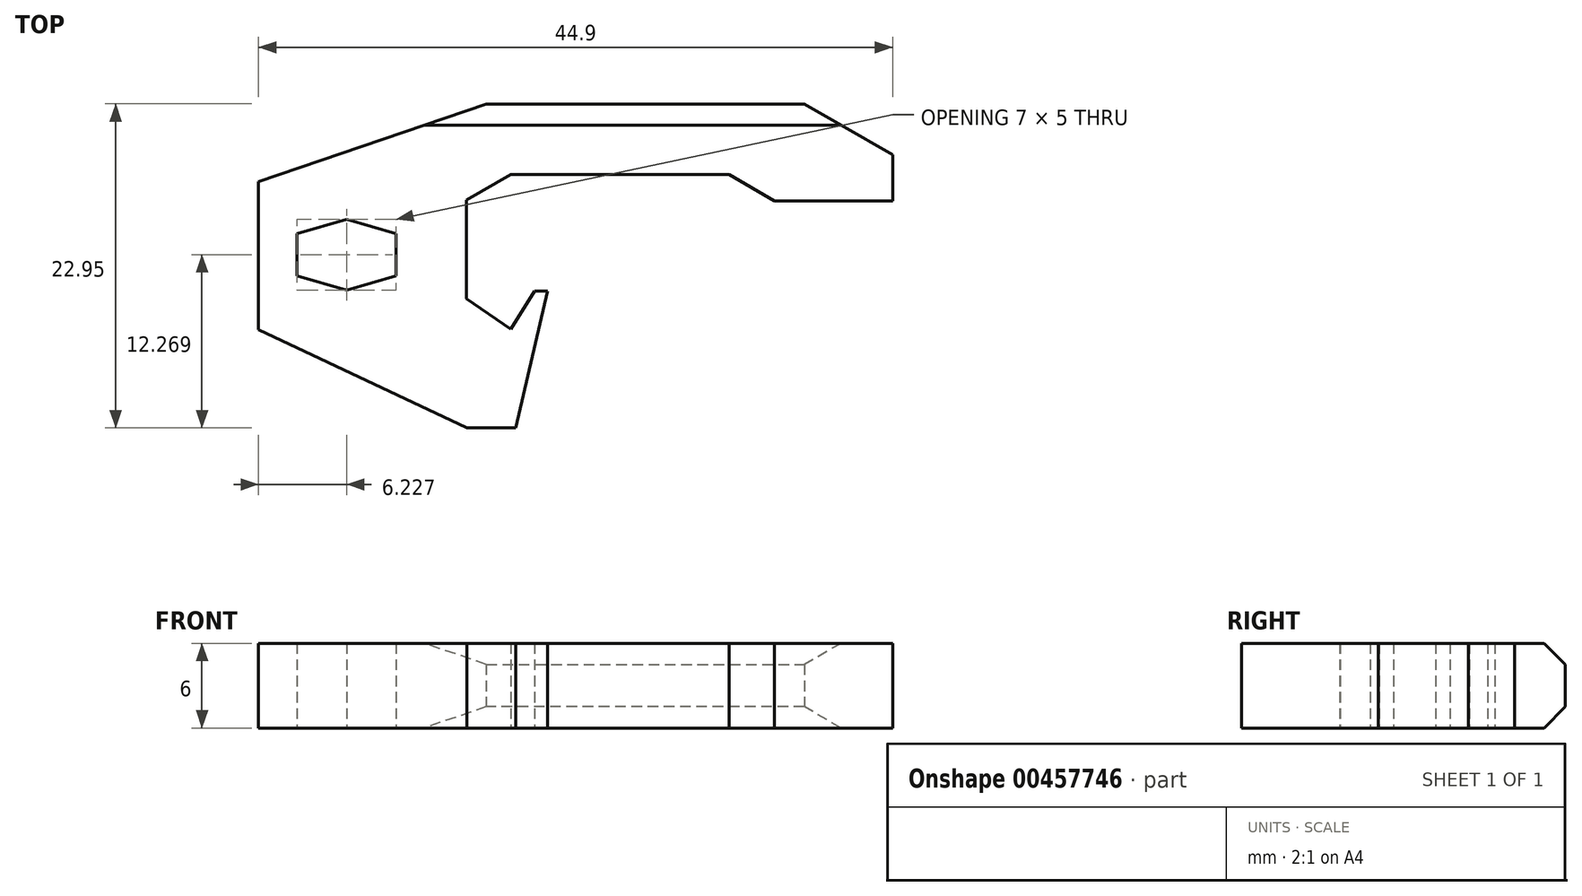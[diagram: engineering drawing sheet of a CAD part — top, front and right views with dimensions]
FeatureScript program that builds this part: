
annotation { "Feature Type Name" : "Feature", "Feature Type Description" : "" }
export const myFeature = defineFeature(function(context is Context, id is Id, definition is map)
    precondition{}
    {
        {
            var Q0;
            Q0=qCreatedBy(makeId("Top.planeOp"),FACE);
            var sketch = newSketch(context, id + "F0", { "sketchPlane" : qUnion([Q0])});
            skLineSegment(sketch, "E0", {"start": v(-1.74, 12.66) * mm, "end": v(20.78, 12.66) * mm});
            skLineSegment(sketch, "E1", {"start": v(20.78, 12.66) * mm, "end": v(32.67, 5.8) * mm});
            skLineSegment(sketch, "E2", {"start": v(32.67, 5.8) * mm, "end": v(18.67, 5.8) * mm});
            skLineSegment(sketch, "E3", {"start": v(18.67, 5.8) * mm, "end": v(15.44, 7.66) * mm});
            skLineSegment(sketch, "E4", {"start": v(15.44, 7.66) * mm, "end": v(0, 7.66) * mm});
            skLineSegment(sketch, "E5", {"start": v(0, 7.66) * mm, "end": v(-3.14, 5.84) * mm});
            skLineSegment(sketch, "E6", {"start": v(-3.14, 5.84) * mm, "end": v(-3.14, -1.15) * mm});
            skLineSegment(sketch, "E7", {"start": v(-3.14, -1.15) * mm, "end": v(0, -3.29) * mm});
            skLineSegment(sketch, "E8", {"start": v(0, -3.29) * mm, "end": v(1.66, -0.58) * mm});
            skLineSegment(sketch, "E9", {"start": v(1.66, -0.58) * mm, "end": v(2.58, -0.58) * mm});
            skLineSegment(sketch, "E10", {"start": v(2.58, -0.58) * mm, "end": v(0.33, -10.29) * mm});
            skLineSegment(sketch, "E11", {"start": v(0.33, -10.29) * mm, "end": v(-3.1, -10.29) * mm});
            skLineSegment(sketch, "E12", {"start": v(-3.1, -10.29) * mm, "end": v(-17.87, -3.32) * mm});
            skLineSegment(sketch, "E13", {"start": v(-17.87, -3.32) * mm, "end": v(-17.87, 7.14) * mm});
            skLineSegment(sketch, "E14", {"start": v(-17.87, 7.14) * mm, "end": v(-1.74, 12.66) * mm});
            skLineSegment(sketch, "E15", {"start": v(-15.14, 3.48) * mm, "end": v(-15.14, 0.48) * mm});
            skLineSegment(sketch, "E16", {"start": v(-15.14, 0.48) * mm, "end": v(-11.64, -0.52) * mm});
            skLineSegment(sketch, "E17", {"start": v(-11.64, -0.52) * mm, "end": v(-8.14, 0.48) * mm});
            skLineSegment(sketch, "E18", {"start": v(-8.14, 0.48) * mm, "end": v(-8.14, 3.48) * mm});
            skLineSegment(sketch, "E19", {"start": v(-8.14, 3.48) * mm, "end": v(-11.64, 4.48) * mm});
            skLineSegment(sketch, "E20", {"start": v(-11.64, 4.48) * mm, "end": v(-15.14, 3.48) * mm});
            skLineSegment(sketch, "E21", {"start": v(-11.64, 4.48) * mm, "end": v(-11.64, -0.52) * mm, "construction": true});
            skLineSegment(sketch, "E22", {"start": v(-15.14, 1.98) * mm, "end": v(-8.14, 1.98) * mm, "construction": true});
            skPoint(sketch, "E23", {"position": v(-11.64, 1.98) * mm});
            skLineSegment(sketch, "E24", {"start": v(27.03, 5.8) * mm, "end": v(27.03, 9.05) * mm});
            skLineSegment(sketch, "E25", {"start": v(-17.87, -2.78) * mm, "end": v(-13.3, -4.32) * mm});
            skLineSegment(sketch, "E26", {"start": v(-13.3, -4.32) * mm, "end": v(-3.1, -10.29) * mm});
            skSolve(sketch);
        }
        {
            var Q0;
            {var subQ0=sQuery(id+"F0.wireOp",EDGE,"E0");Q0=makeQuery(id+"F0.imprint","IMPRINT",FACE,{"disambiguationData":[TD([[makeQuery(id+"F0.imprint","IMPRINT",EDGE,{"derivedFrom":subQ0}),-1.0]])]});}
            var Q1;
            {var subQ0=sQuery(id+"F0.wireOp",EDGE,"E12");Q1=makeQuery(id+"F0.imprint","IMPRINT",FACE,{"disambiguationData":[TD([[makeQuery(id+"F0.imprint","IMPRINT",EDGE,{"derivedFrom":subQ0}),-1.0]])]});}
            extrude(context, id + "F1", {"entities" : qUnion([Q0, Q1]), "depth" : 6 * mm});
        }
        {
            var Q0;
            Q0=makeQuery(id+"F1.opExtrude","CAP_EDGE",EDGE,{"disambiguationData":[OSD([sQuery(id+"F0.wireOp",EDGE,"E0")])],"isStart":false});
            var Q1;
            Q1=makeQuery(id+"F1.opExtrude","CAP_EDGE",EDGE,{"disambiguationData":[OSD([sQuery(id+"F0.wireOp",EDGE,"E0")])],"isStart":true});
            chamfer(context, id + "F2", {"entities" : qUnion([Q0, Q1]), "width" : 1.5 * mm, "tangentPropagation" : true});
        }
    });
